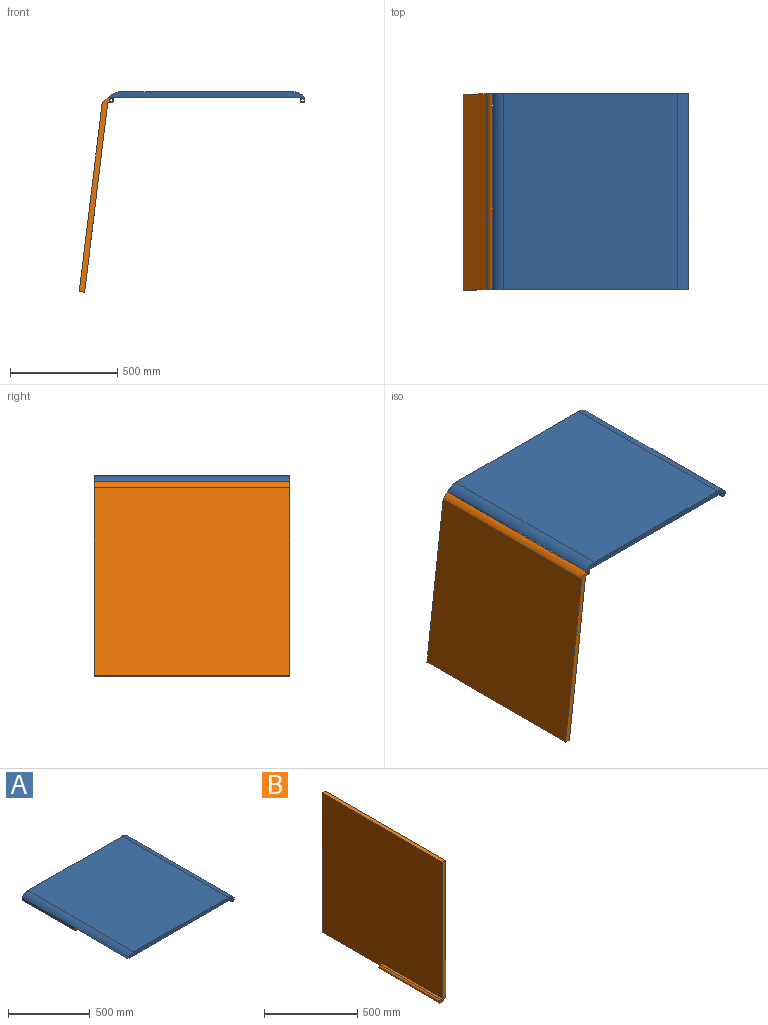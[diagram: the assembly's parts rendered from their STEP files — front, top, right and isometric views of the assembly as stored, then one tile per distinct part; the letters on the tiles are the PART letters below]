
ASSEMBLY  parts=2 mates=1
PART A: 16 faces, bbox 914.4x914.4x50.8 mm
  f0: plane 914.4x914.4mm, normal (0,0,-1), area 816617.7mm2, adj f1,f2,f4,f5,f7,f9,f12,f15
  f1: plane 914.4x50.8mm, normal (0,1,0), area 22749.2mm2, adj f0,f3,f4,f5,f6,f8,f9,f10
  f2: plane 914.4x50.8mm, normal (0,-1,0), area 22749.2mm2, adj f0,f3,f4,f5,f11,f12,f13,f14
  f3: plane 914.4x811.7mm, normal (0,0,1), area 742215.8mm2, adj f1,f2,f4,f5
  f4: cylinder r=64.61mm len=914.4mm, axis (0,-1,0), area 54274.5mm2, adj f0,f1,f2,f3,f11
  f5: cylinder r=64.61mm len=914.4mm, axis (0,-1,0), area 54274.5mm2, adj f0,f1,f2,f3,f6
  f6: plane 457.2x14.73mm, normal (-1,0,0), area 6735.5mm2, adj f1,f5,f7,f8
  f7: plane 25.4x21.34mm, normal (0,-1,0), area 310.7mm2, adj f0,f6,f8,f9,f10
  f8: cylinder r=10.67mm len=457.2mm, axis (0,-1,0), area 15322.8mm2, adj f1,f6,f7,f9
  f9: plane 457.2x14.73mm, normal (1,0,0), area 6735.5mm2, adj f0,f1,f7,f8
  f10: cylinder r=7.62mm len=457.2mm, axis (0,-1,0), area 21889.8mm2, adj f1,f7
  f11: plane 457.2x14.73mm, normal (1,0,0), area 6735.5mm2, adj f2,f4,f13,f15
  f12: plane 457.2x14.73mm, normal (-1,0,0), area 6735.5mm2, adj f0,f2,f13,f15
  f13: cylinder r=10.67mm len=457.2mm, axis (0,1,0), area 15322.8mm2, adj f2,f11,f12,f15
  f14: cylinder r=7.62mm len=457.2mm, axis (0,1,0), area 21889.8mm2, adj f2,f15
  f15: plane 25.4x21.34mm, normal (0,1,0), area 310.7mm2, adj f0,f11,f12,f13,f14
PART B: 11 faces, bbox 50.8x914.4x914.4 mm
  f0: plane 457.2x14.73mm, normal (0,0,-1), area 6735.5mm2, adj f1,f8,f9,f10
  f1: plane 914.4x50.8mm, normal (0,-1,0), area 23224.2mm2, adj f0,f2,f4,f5,f6,f7,f8,f10
  f2: plane 914.4x914.4mm, normal (-1,0,0), area 826372.5mm2, adj f1,f3,f4,f6,f9,f10
  f3: plane 914.4x25.4mm, normal (0,1,0), area 22913.6mm2, adj f2,f4,f5,f10
  f4: plane 914.4x25.4mm, normal (0,0,1), area 23225.8mm2, adj f1,f2,f3,f5
  f5: plane 914.4x882.86mm, normal (1,0,0), area 807290.5mm2, adj f1,f3,f4,f10
  f6: plane 457.2x14.73mm, normal (0,0,1), area 6735.5mm2, adj f1,f2,f8,f9
  f7: cylinder r=7.62mm len=457.2mm, axis (0,1,0), area 21889.8mm2, adj f1,f9
  f8: cylinder r=10.67mm len=457.2mm, axis (0,1,0), area 15322.8mm2, adj f0,f1,f6,f9
  f9: plane 25.4x21.34mm, normal (0,1,0), area 310.7mm2, adj f0,f2,f6,f7,f8
  f10: cylinder r=64.61mm len=914.4mm, axis (0,-1,0), area 37661.5mm2, adj f0,f1,f2,f3,f5
PLACE A at identity fixed
PLACE B rot(axis=(0,-1,0),173.1deg) t=(-515.11,0,432.79)mm
MATE revolute A.f8 <-> B.f7  axis (0,-1,0) through (-446.53,0,874.27)mm
